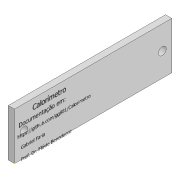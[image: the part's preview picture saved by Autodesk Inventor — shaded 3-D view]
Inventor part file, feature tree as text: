
AUTODESK INVENTOR PART (.ipt)
format: ipt  version: 2020 (Build 240168000, 168)  size: 95,744 bytes
history: native  units: mm
features: sketch x3, extrude x2, other x1
ambient origin geometry x8: Origin, YZ Plane, XZ Plane, XY Plane, X Axis, Y Axis, Z Axis, Center Point
bodies: Body1 (feature_tree)
feature tree (6):
  other  "Sólido1"
  extrude  "Extrusão1"  Depth=30.0mm
  sketch  "Esboço2"  dims[d2=4.0mm d3=0.0mm d4=5.0mm]
  extrude  "Extrusão2"  Depth=4.0mm
  sketch  "Esboço1"  dims[d0=100.0mm d1=30.0mm]
  sketch  "Esboço3"  dims[d5=5.0mm d6=6.0mm d7=6.0mm d8=4.0mm d9=0.0mm]
